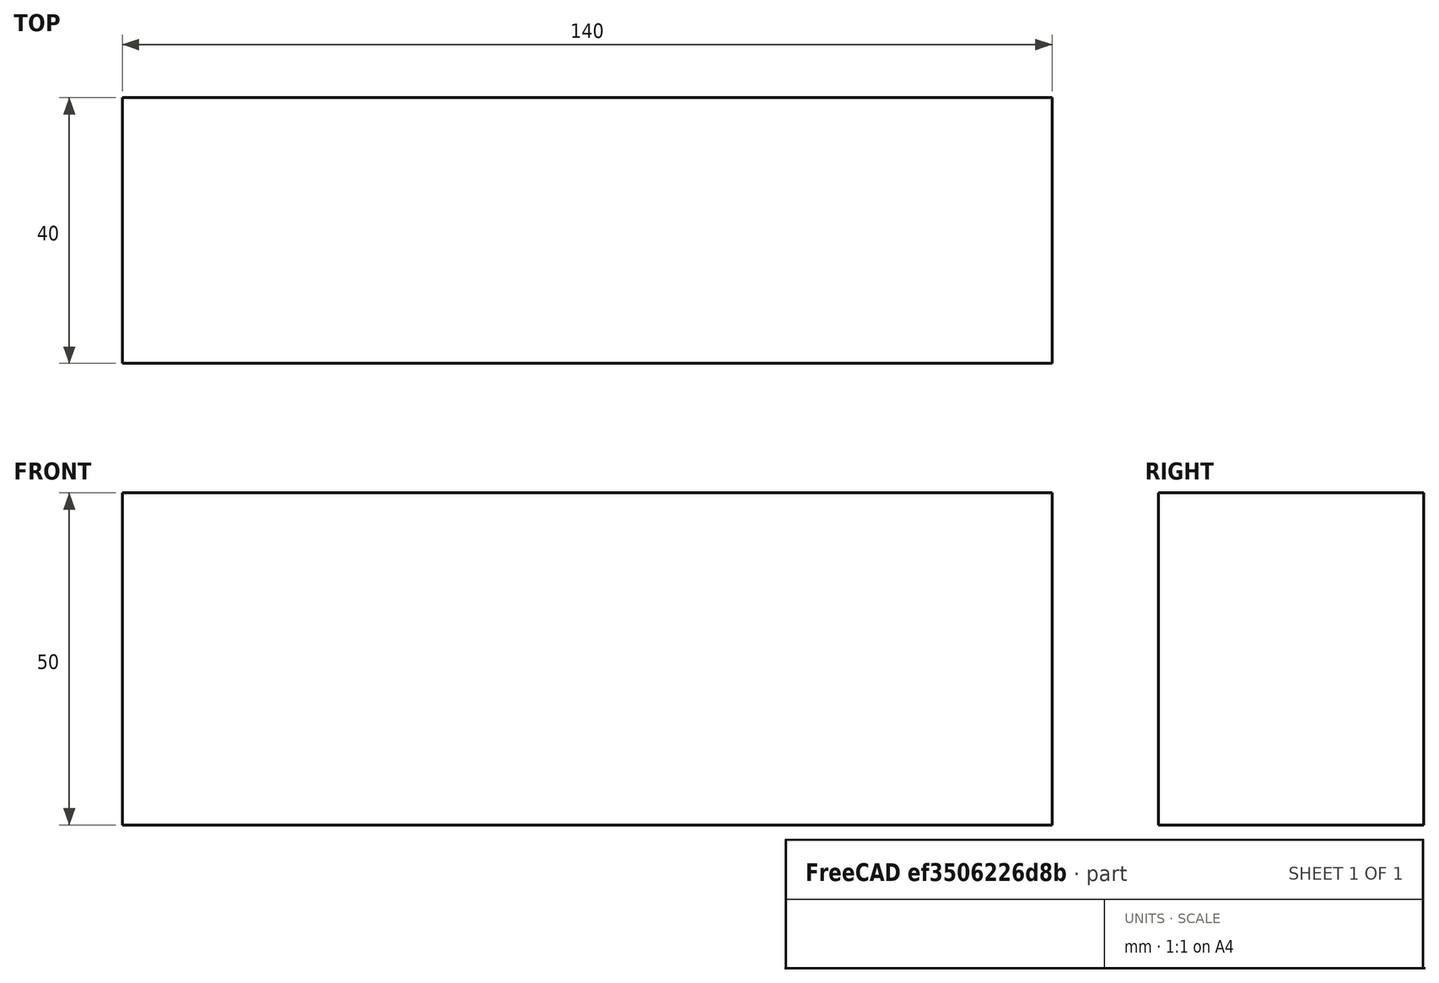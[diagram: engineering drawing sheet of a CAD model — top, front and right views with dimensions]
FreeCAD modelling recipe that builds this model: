
FCSTD DOCUMENT  (FreeCAD 0.15R4671 (Git))
Label: Flat Bar 140x40 EN10058 S235JR
License: All rights reserved
LicenseURL: http://en.wikipedia.org/wiki/All_rights_reserved
objects: Sketcher::SketchObject×1, Part::Extrusion×1
note: 2 computed .brp shape members not serialized (recipe doc carries the construction recipe); baked Part::Feature solids carry a one-line shape summary decoded from their .brp

FEATURE [Sketcher::SketchObject] Sketch
  sketch-geometry (4):
    g0: LineSegment StartX=-70 StartY=-20 StartZ=0 EndX=70 EndY=-20 EndZ=0
    g1: LineSegment StartX=70 StartY=-20 StartZ=0 EndX=70 EndY=20 EndZ=0
    g2: LineSegment StartX=70 StartY=20 StartZ=0 EndX=-70 EndY=20 EndZ=0
    g3: LineSegment StartX=-70 StartY=20 StartZ=0 EndX=-70 EndY=-20 EndZ=0
  constraints (12):
    c: Coincident(g0,g1)
    c: Coincident(g1,g2)
    c: Coincident(g2,g3)
    c: Coincident(g3,g0)
    c: Horizontal(g0)
    c: Horizontal(g2)
    c: Vertical(g1)
    c: Vertical(g3)
    c: Symmetric(g1,g2,g-2)
    c: Symmetric(g0,g1,g-1)
    c: DistanceY(g1) = 40
    c: DistanceX(g0) = 140
FEATURE [Part::Extrusion] Extrude  label="Flat Bar 140x40 EN10058 S235JR"
  Base = -> Sketch
  Dir = (0,0,50)
  Solid = true
